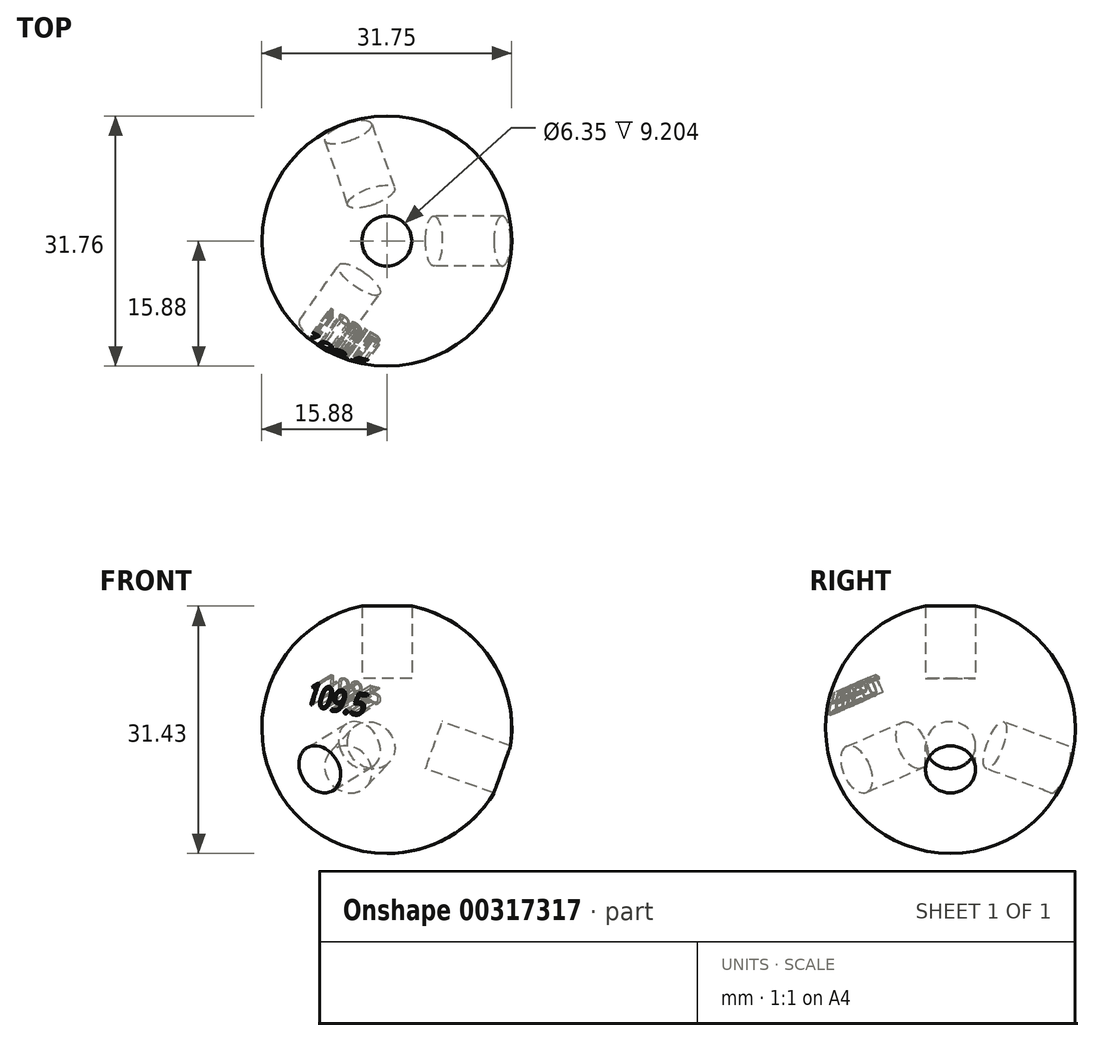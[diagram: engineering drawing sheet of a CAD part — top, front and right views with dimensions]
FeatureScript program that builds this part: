
annotation { "Feature Type Name" : "Feature", "Feature Type Description" : "" }
export const myFeature = defineFeature(function(context is Context, id is Id, definition is map)
    precondition{}
    {
        {
            var Q0;
            Q0=qCreatedBy(makeId("Front.planeOp"),FACE);
            var sketch = newSketch(context, id + "F0", { "sketchPlane" : qUnion([Q0])});
            skArc(sketch, "E0", {"start": v(0, 15.88) * mm, "mid": v(-15.88, 0) * mm, "end": v(0, -15.88) * mm});
            skLineSegment(sketch, "E1", {"start": v(0, 15.88) * mm, "end": v(0, -15.88) * mm});
            skSolve(sketch);
        }
        {
            var Q0;
            Q0=qCreatedBy(makeId("Top.planeOp"),FACE);
            var sketch = newSketch(context, id + "F1", { "sketchPlane" : qUnion([Q0])});
            skCircle(sketch, "E2", {"center": v(0, 0) * mm, "radius": 15.88 * mm});
            skSolve(sketch);
        }
        {
            var Q0;
            Q0=makeQuery(id+"F0.imprint","IMPRINT",FACE,{"disambiguationData":[TD([[makeQuery(id+"F0.imprint","IMPRINT",EDGE,{"derivedFrom":sQuery(id+"F0.wireOp",EDGE,"E0")}),1.0]])]});
            var Q1;
            Q1=sQuery(id+"F1.wireOp",EDGE,"E2");
            revolve(context, id + "F2", {"entities" : qUnion([Q0]), "axis" : qUnion([Q1]), "revolveType" : RevolveType.FULL});
        }
        {
            var Q0;
            Q0=qCreatedBy(makeId("Front.planeOp"),FACE);
            var sketch = newSketch(context, id + "F3", { "sketchPlane" : qUnion([Q0])});
            skLineSegment(sketch, "E3", {"start": v(0, 0) * mm, "end": v(75.21, 0) * mm, "construction": true});
            skLineSegment(sketch, "E4", {"start": v(0, 0) * mm, "end": v(0, 67.91) * mm, "construction": true});
            skSolve(sketch);
        }
        {
            var Q0;
            Q0=qCreatedBy(makeId("Top.planeOp"),FACE);
            var sketch = newSketch(context, id + "F4", { "sketchPlane" : qUnion([Q0])});
            skLineSegment(sketch, "E5", {"start": v(0, 0) * mm, "end": v(0, 73.58) * mm, "construction": true});
            skSolve(sketch);
        }
        {
            var Q0;
            Q0=qCreatedBy(makeId("Top.planeOp"),FACE);
            cPlane(context, id + "F5", {"entities" : qUnion([Q0]), "cplaneType" : CPlaneType.OFFSET, "offset" : 6.35 * mm, "width" : 152.4 * mm, "height" : 152.4 * mm});
        }
        {
            var Q0;
            Q0=qCreatedBy(id+"F5.planeOp",FACE);
            var sketch = newSketch(context, id + "F6", { "sketchPlane" : qUnion([Q0])});
            skCircle(sketch, "E6", {"center": v(0, 0) * mm, "radius": 3.18 * mm});
            skSolve(sketch);
        }
        {
            var Q0;
            Q0 = qSketchRegion(id + "F6", true);
            extrude(context, id + "F7", {"entities" : qUnion([Q0]), "depth" : 38.1 * mm});
        }
        {
            var Q0;
            Q0=makeQuery(id+"F7.opExtrude","SWEPT_BODY",BODY,{"disambiguationData":[OSD([sQuery(id+"F6.wireOp",EDGE,"E6")])]});
            var Q1;
            Q1=sQuery(id+"F4.wireOp",EDGE,"E5");
            transform(context, id + "F8", {"entities" : qUnion([Q0]), "transformType" : TransformType.ROTATION, "transformAxis" : qUnion([Q1]), "angle" : 109.5 * degree, "makeCopy" : true});
        }
        {
            var Q0;
            Q0=makeQuery(id+"F8.opPattern","COPY",BODY,{"derivedFrom":makeQuery(id+"F7.opExtrude","SWEPT_BODY",BODY,{"disambiguationData":[OSD([sQuery(id+"F6.wireOp",EDGE,"E6")])]}),"instanceName":"1"});
            var Q1;
            Q1=sQuery(id+"F3.wireOp",EDGE,"E4");
            transform(context, id + "F9", {"entities" : qUnion([Q0]), "transformType" : TransformType.ROTATION, "transformAxis" : qUnion([Q1]), "angle" : 109.5 * degree, "makeCopy" : true});
        }
        {
            var Q0;
            Q0=makeQuery(id+"F9.opPattern","COPY",BODY,{"derivedFrom":makeQuery(id+"F8.opPattern","COPY",BODY,{"derivedFrom":makeQuery(id+"F7.opExtrude","SWEPT_BODY",BODY,{"disambiguationData":[OSD([sQuery(id+"F6.wireOp",EDGE,"E6")])]}),"instanceName":"1"}),"instanceName":"1"});
            var Q1;
            Q1=makeQuery(id+"F7.opExtrude","CAP_EDGE",EDGE,{"disambiguationData":[OSD([sQuery(id+"F6.wireOp",EDGE,"E6")])],"isStart":false});
            transform(context, id + "F10", {"entities" : qUnion([Q0]), "transformType" : TransformType.ROTATION, "transformAxis" : qUnion([Q1]), "angle" : 125 * degree, "makeCopy" : true});
        }
        {
            var Q0;
            Q0=makeQuery(id+"F10.opPattern","COPY",FACE,{"derivedFrom":makeQuery(id+"F9.opPattern","COPY",FACE,{"derivedFrom":makeQuery(id+"F8.opPattern","COPY",FACE,{"derivedFrom":makeQuery(id+"F7.opExtrude","CAP_FACE",FACE,{"disambiguationData":[OSD([sQuery(id+"F6.wireOp",EDGE,"E6")])],"isStart":false}),"instanceName":"1"}),"instanceName":"1"}),"instanceName":"1"});
            cPlane(context, id + "F11", {"entities" : qUnion([Q0]), "cplaneType" : CPlaneType.OFFSET, "offset" : 25.4 * mm, "oppositeDirection" : true, "width" : 152.4 * mm, "height" : 152.4 * mm});
        }
        {
            var Q0;
            Q0=qCreatedBy(id+"F11.planeOp",FACE);
            var sketch = newSketch(context, id + "F12", { "sketchPlane" : qUnion([Q0])});
            skText(sketch, "E7", { "text": "109.5\n", "fontName": "OpenSans-Regular.ttf"});
            const initialGuessF12  = {"E7": [-0.00352, 0.00767, 1, 0, 0.0024]};
            skSetInitialGuess(sketch, initialGuessF12);
            skSolve(sketch);
        }
        {
            var Q0;
            Q0 = qSketchRegion(id + "F12", true);
            extrude(context, id + "F13", {"entities" : qUnion([Q0]), "operationType" : NewBodyOperationType.REMOVE, "oppositeDirection" : true, "depth" : 10.16 * mm});
        }
        {
            var Q0;
            Q0=makeQuery(id+"F7.opExtrude","SWEPT_BODY",BODY,{"disambiguationData":[OSD([sQuery(id+"F6.wireOp",EDGE,"E6")])]});
            var Q1;
            Q1=makeQuery(id+"F10.opPattern","COPY",BODY,{"derivedFrom":makeQuery(id+"F9.opPattern","COPY",BODY,{"derivedFrom":makeQuery(id+"F8.opPattern","COPY",BODY,{"derivedFrom":makeQuery(id+"F7.opExtrude","SWEPT_BODY",BODY,{"disambiguationData":[OSD([sQuery(id+"F6.wireOp",EDGE,"E6")])]}),"instanceName":"1"}),"instanceName":"1"}),"instanceName":"1"});
            var Q2;
            Q2=makeQuery(id+"F9.opPattern","COPY",BODY,{"derivedFrom":makeQuery(id+"F8.opPattern","COPY",BODY,{"derivedFrom":makeQuery(id+"F7.opExtrude","SWEPT_BODY",BODY,{"disambiguationData":[OSD([sQuery(id+"F6.wireOp",EDGE,"E6")])]}),"instanceName":"1"}),"instanceName":"1"});
            var Q3;
            Q3=makeQuery(id+"F8.opPattern","COPY",BODY,{"derivedFrom":makeQuery(id+"F7.opExtrude","SWEPT_BODY",BODY,{"disambiguationData":[OSD([sQuery(id+"F6.wireOp",EDGE,"E6")])]}),"instanceName":"1"});
            var Q4;
            Q4=makeQuery(id+"F2.opRevolve","SWEPT_BODY",BODY,{"disambiguationData":[OSD([sQuery(id+"F0.wireOp",EDGE,"E0"),sQuery(id+"F0.wireOp",EDGE,"E1")])]});
            booleanBodies(context, id + "F14", {"operationType" : BooleanOperationType.SUBTRACTION, "tools" : qUnion([Q0, Q1, Q2, Q3]), "targets" : qUnion([Q4])});
        }
    });
